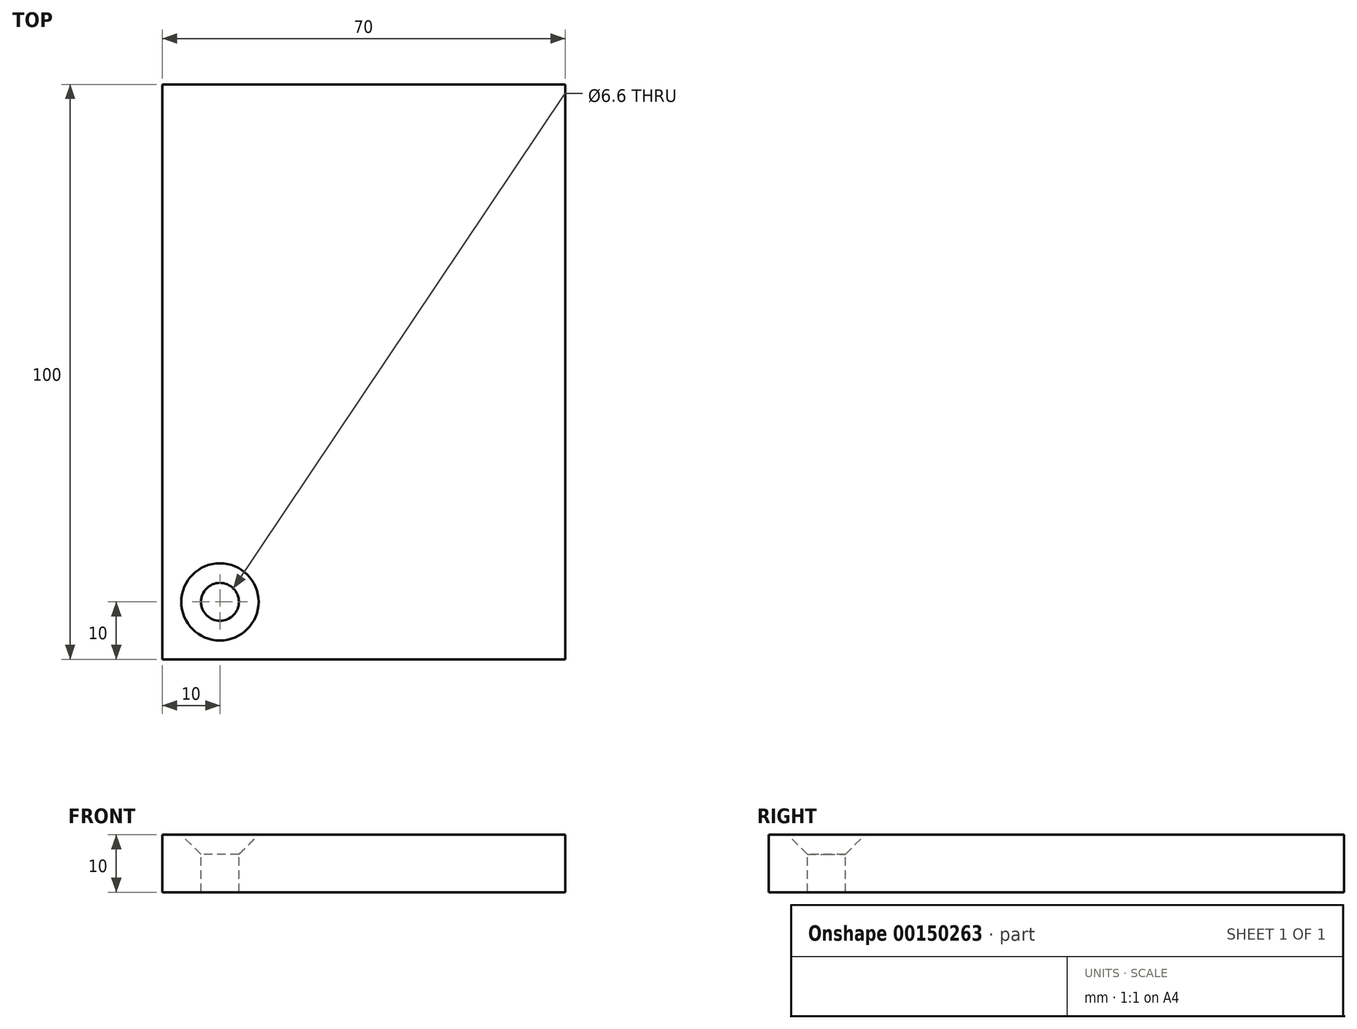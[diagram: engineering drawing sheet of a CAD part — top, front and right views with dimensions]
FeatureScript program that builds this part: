
annotation { "Feature Type Name" : "Feature", "Feature Type Description" : "" }
export const myFeature = defineFeature(function(context is Context, id is Id, definition is map)
    precondition{}
    {
        {
            var Q0;
            Q0=qCreatedBy(makeId("Top.planeOp"),FACE);
            var sketch = newSketch(context, id + "F0", { "sketchPlane" : qUnion([Q0])});
            skLineSegment(sketch, "E0.bottom", {"start": v(-35, -10) * mm, "end": v(35, -10) * mm});
            skLineSegment(sketch, "E0.top", {"start": v(-35, 90) * mm, "end": v(35, 90) * mm});
            skLineSegment(sketch, "E0.left", {"start": v(-35, -10) * mm, "end": v(-35, 90) * mm});
            skLineSegment(sketch, "E0.right", {"start": v(35, -10) * mm, "end": v(35, 90) * mm});
            skSolve(sketch);
        }
        {
            var Q0;
            Q0 = qSketchRegion(id + "F0", true);
            extrude(context, id + "F1", {"entities" : qUnion([Q0]), "depth" : 10 * mm});
        }
        {
            var Q0;
            Q0=makeQuery(id+"F1.opExtrude","CAP_FACE",FACE,{"disambiguationData":[OSD([sQuery(id+"F0.wireOp",EDGE,"E0.bottom"),sQuery(id+"F0.wireOp",EDGE,"E0.top"),sQuery(id+"F0.wireOp",EDGE,"E0.left"),sQuery(id+"F0.wireOp",EDGE,"E0.right")])],"isStart":false});
            var sketch = newSketch(context, id + "F2", { "sketchPlane" : qUnion([Q0])});
            skPoint(sketch, "E1", {"position": v(-25, 0) * mm});
            skSolve(sketch);
        }
        {
            var Q0;
            Q0=sQuery(id+"F2.wireOp",VERTEX,"E1");
            var Q1;
            Q1=makeQuery(id+"F1.opExtrude","SWEPT_BODY",BODY,{"disambiguationData":[OSD([sQuery(id+"F0.wireOp",EDGE,"E0.bottom"),sQuery(id+"F0.wireOp",EDGE,"E0.top"),sQuery(id+"F0.wireOp",EDGE,"E0.left"),sQuery(id+"F0.wireOp",EDGE,"E0.right")])]});
            hole(context, id + "F3", {"style" : HoleStyle.C_SINK, "endStyle" : HoleEndStyle.THROUGH, "standardTappedOrClearance" : lookupTablePath({ "standard" : "ISO", "fit" : "Normal", "size" : "M6", "type" : "Clearance" }), "standardBlindInLast" : lookupTablePath({ "fit" : "Standard", "standard" : "ISO", "size" : "M6", "type" : "Clearance" }), "holeDiameter" : 6.6 * mm, "cSinkDiameter" : 13.44 * mm, "cSinkAngle" : 90 * degree, "locations" : qUnion([Q0]), "scope" : qUnion([Q1]), "isTappedThrough" : true});
        }
    });
